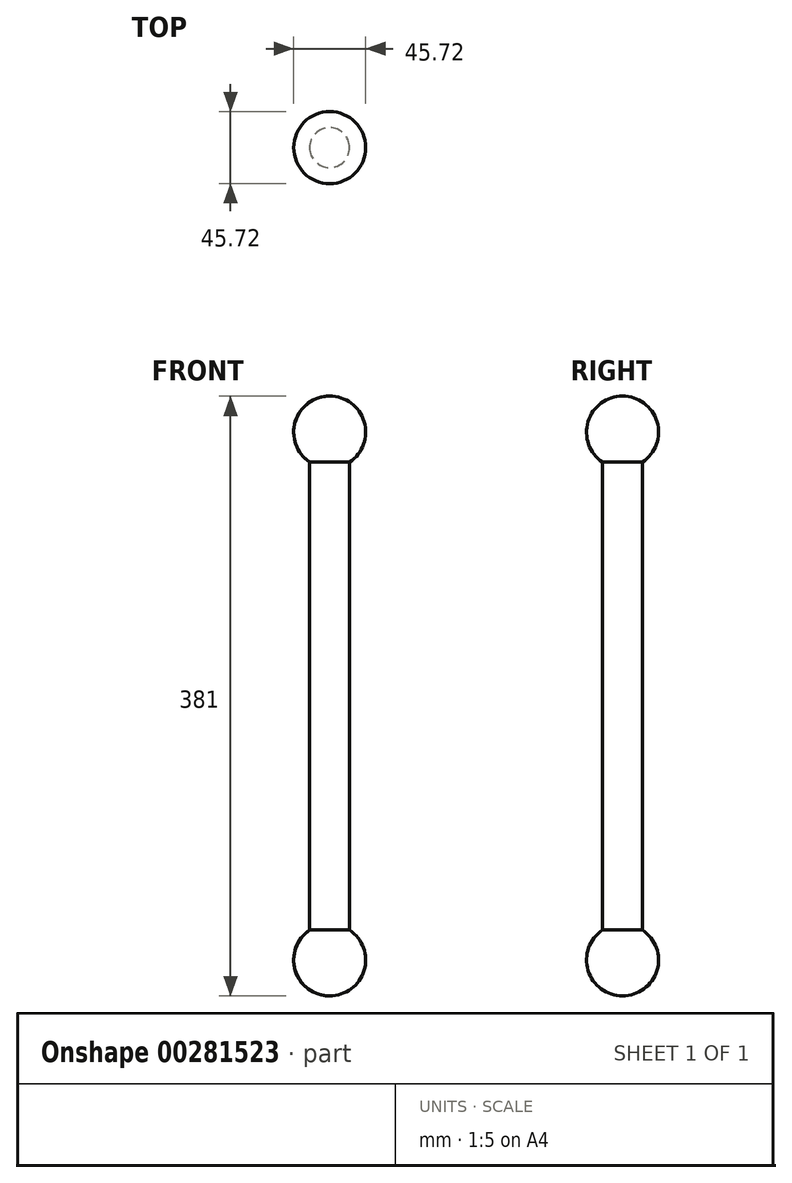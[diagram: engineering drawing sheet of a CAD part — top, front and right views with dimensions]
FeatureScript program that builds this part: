
annotation { "Feature Type Name" : "Feature", "Feature Type Description" : "" }
export const myFeature = defineFeature(function(context is Context, id is Id, definition is map)
    precondition{}
    {
        {
            var Q0;
            Q0=qCreatedBy(makeId("Front.planeOp"),FACE);
            var sketch = newSketch(context, id + "F0", { "sketchPlane" : qUnion([Q0])});
            skLineSegment(sketch, "E0", {"start": v(0, 190.5) * mm, "end": v(0, -190.5) * mm});
            skArc(sketch, "E1", {"start": v(0, 190.5) * mm, "mid": v(-21.88, 174.28) * mm, "end": v(-12.7, 148.63) * mm});
            skArc(sketch, "E2.MirrorCS", {"start": v(0, -190.5) * mm, "mid": v(-21.88, -174.28) * mm, "end": v(-12.7, -148.63) * mm});
            skLineSegment(sketch, "E3", {"start": v(-12.7, 148.63) * mm, "end": v(-12.7, -148.63) * mm});
            skSolve(sketch);
        }
        {
            var Q0;
            Q0 = qSketchRegion(id + "F0", true);
            var Q1;
            Q1=sQuery(id+"F0.wireOp",EDGE,"E0");
            revolve(context, id + "F1", {"entities" : qUnion([Q0]), "axis" : qUnion([Q1]), "revolveType" : RevolveType.FULL});
        }
    });
